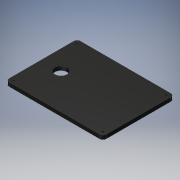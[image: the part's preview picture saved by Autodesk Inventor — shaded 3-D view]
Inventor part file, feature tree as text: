
AUTODESK INVENTOR PART (.ipt)
format: ipt  version: 2019 (Build 230136000, 136)  size: 129,024 bytes
history: native  units: mm
features: extrude x3, sketch x3
ambient origin geometry x8: Origin, YZ Plane, XZ Plane, XY Plane, X Axis, Y Axis, Z Axis, Center Point
bodies: Solid1 (feature_tree)
feature tree (6):
  extrude  "Extrusion1"  Depth=6.0mm
  extrude  "Extrusion2"  Depth=3.3mm
  extrude  "Extrusion3"  Depth=6.0mm TaperAngle=0.0deg
  sketch  "Sketch1"  dims[d0=6.0mm d1=0.0mm d2=3.3mm]
  sketch  "Sketch2"  dims[d3=3.3mm d4=3.3mm]
  sketch  "Sketch3"  dims[d5=3.3mm d6=6.0mm d7=0.0mm d8=18.8mm d9=30.0mm d10=55.0mm d11=6.0mm d12=0.0mm]
